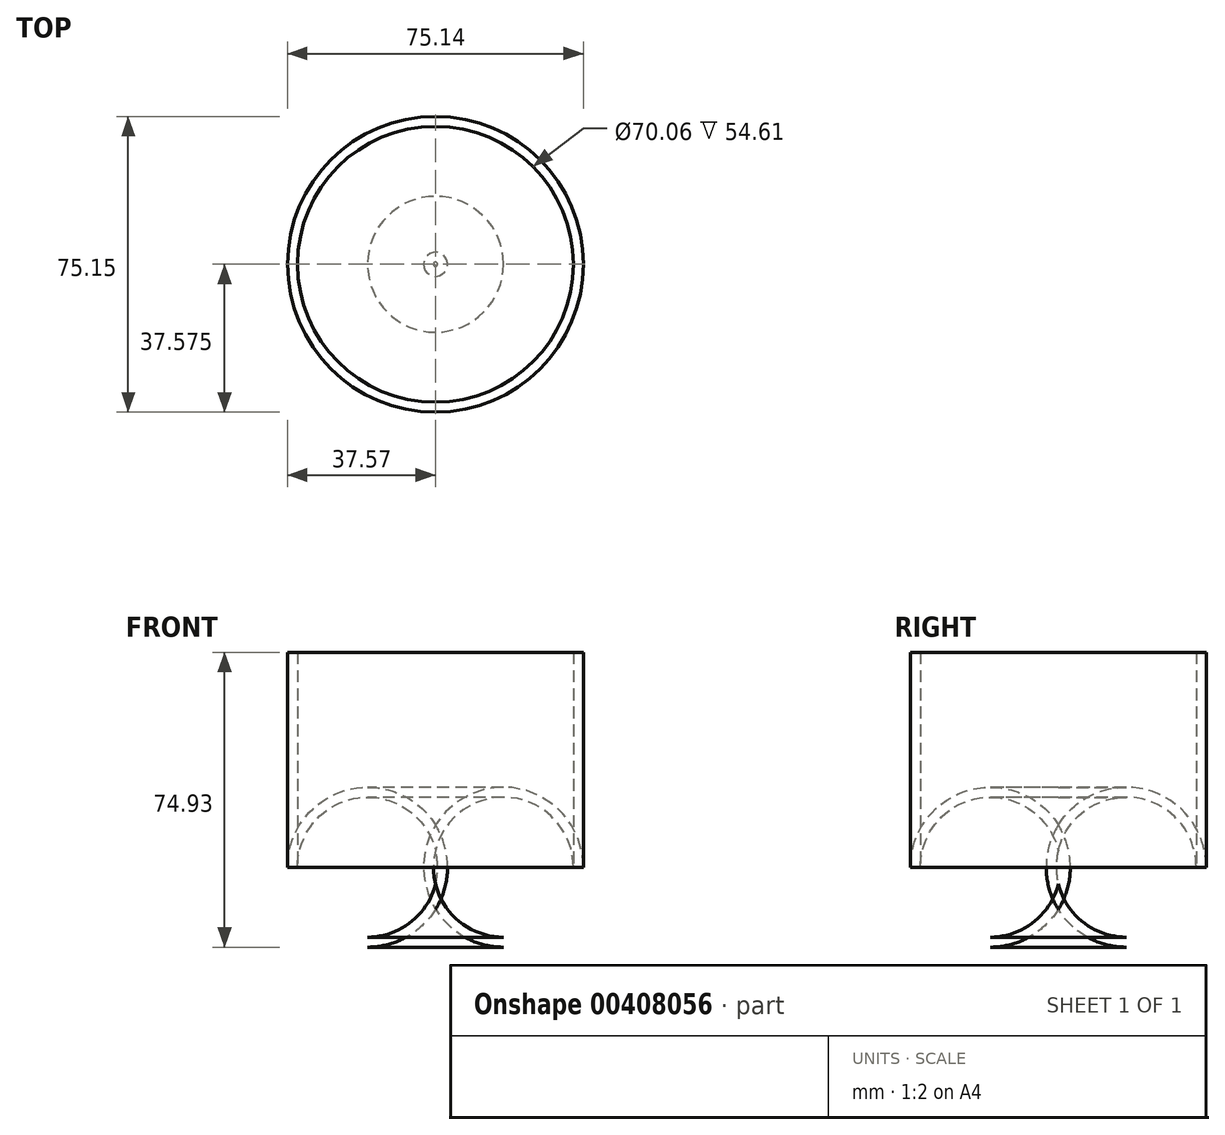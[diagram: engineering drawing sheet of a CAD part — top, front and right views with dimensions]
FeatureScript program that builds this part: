
annotation { "Feature Type Name" : "Feature", "Feature Type Description" : "" }
export const myFeature = defineFeature(function(context is Context, id is Id, definition is map)
    precondition{}
    {
        {
            var Q0;
            Q0=qCreatedBy(makeId("Top.planeOp"),FACE);
            var sketch = newSketch(context, id + "F0", { "sketchPlane" : qUnion([Q0])});
            skCircle(sketch, "E0", {"center": v(-13.78, 12.51) * mm, "radius": 37.57 * mm});
            skSolve(sketch);
        }
        {
            var Q0;
            Q0 = qSketchRegion(id + "F0", true);
            extrude(context, id + "F1", {"entities" : qUnion([Q0]), "depth" : 74.93 * mm});
        }
        {
            var Q0;
            Q0=makeQuery(id+"F1.opExtrude","CAP_FACE",FACE,{"disambiguationData":[OSD([sQuery(id+"F0.wireOp",EDGE,"E0")])],"isStart":true});
            fillet(context, id + "F2", {"entities" : qUnion([Q0]), "radius" : 20.32 * mm, "tangentPropagation" : true, "allowEdgeOverflow" : false});
        }
        {
            var Q0;
            Q0=makeQuery(id+"F1.opExtrude","CAP_FACE",FACE,{"disambiguationData":[OSD([sQuery(id+"F0.wireOp",EDGE,"E0")])],"isStart":false});
            shell(context, id + "F3", {"entities" : qUnion([Q0]), "thickness" : 2.54 * mm});
        }
    });
